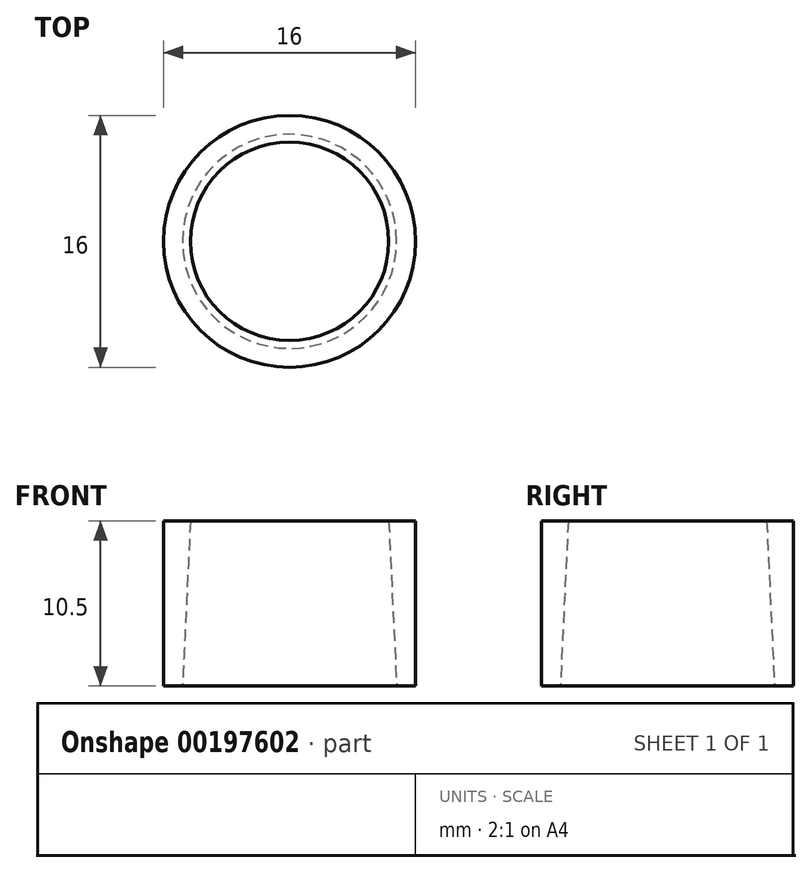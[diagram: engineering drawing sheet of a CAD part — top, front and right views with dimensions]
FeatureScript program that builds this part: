
annotation { "Feature Type Name" : "Feature", "Feature Type Description" : "" }
export const myFeature = defineFeature(function(context is Context, id is Id, definition is map)
    precondition{}
    {
        {
            var Q0;
            Q0=qCreatedBy(makeId("Top.planeOp"),FACE);
            var sketch = newSketch(context, id + "F0", { "sketchPlane" : qUnion([Q0])});
            skCircle(sketch, "E0", {"center": v(0, 0) * mm, "radius": 6.3 * mm});
            skCircle(sketch, "E1", {"center": v(0, 0) * mm, "radius": 8 * mm});
            skCircle(sketch, "E2", {"center": v(0, 0) * mm, "radius": 6.8 * mm});
            skSolve(sketch);
        }
        {
            var Q0;
            Q0=qCreatedBy(makeId("Front.planeOp"),FACE);
            var sketch = newSketch(context, id + "F1", { "sketchPlane" : qUnion([Q0])});
            skLineSegment(sketch, "E3.0", {"start": v(-6.8, 0) * mm, "end": v(6.8, 0) * mm});
            skLineSegment(sketch, "E4.0", {"start": v(-6.3, 0) * mm, "end": v(6.3, 0) * mm});
            skLineSegment(sketch, "E5.0", {"start": v(-8, 0) * mm, "end": v(-5.58, 0) * mm});
            skLineSegment(sketch, "E6", {"start": v(0, 0) * mm, "end": v(0, 10.5) * mm});
            skLineSegment(sketch, "E7.top", {"start": v(-8, 10.5) * mm, "end": v(-6.3, 10.5) * mm});
            skLineSegment(sketch, "E7.left", {"start": v(-8, 0) * mm, "end": v(-8, 10.5) * mm});
            skLineSegment(sketch, "E8", {"start": v(-6.3, 10.5) * mm, "end": v(-6.8, 0) * mm});
            skLineSegment(sketch, "E9.trimOffspring", {"start": v(0, 0) * mm, "end": v(8, 0) * mm});
            skSolve(sketch);
        }
        {
            var Q0;
            Q0=makeQuery(id+"F1.imprint","IMPRINT",FACE,{"disambiguationData":[TD([[makeQuery(id+"F1.imprint","IMPRINT",EDGE,{"derivedFrom":sQuery(id+"F1.wireOp",EDGE,"E7.top")}),-1.0]])]});
            var Q1;
            Q1=sQuery(id+"F1.wireOp",EDGE,"E6");
            revolve(context, id + "F2", {"entities" : qUnion([Q0]), "axis" : qUnion([Q1]), "revolveType" : RevolveType.FULL});
        }
    });
